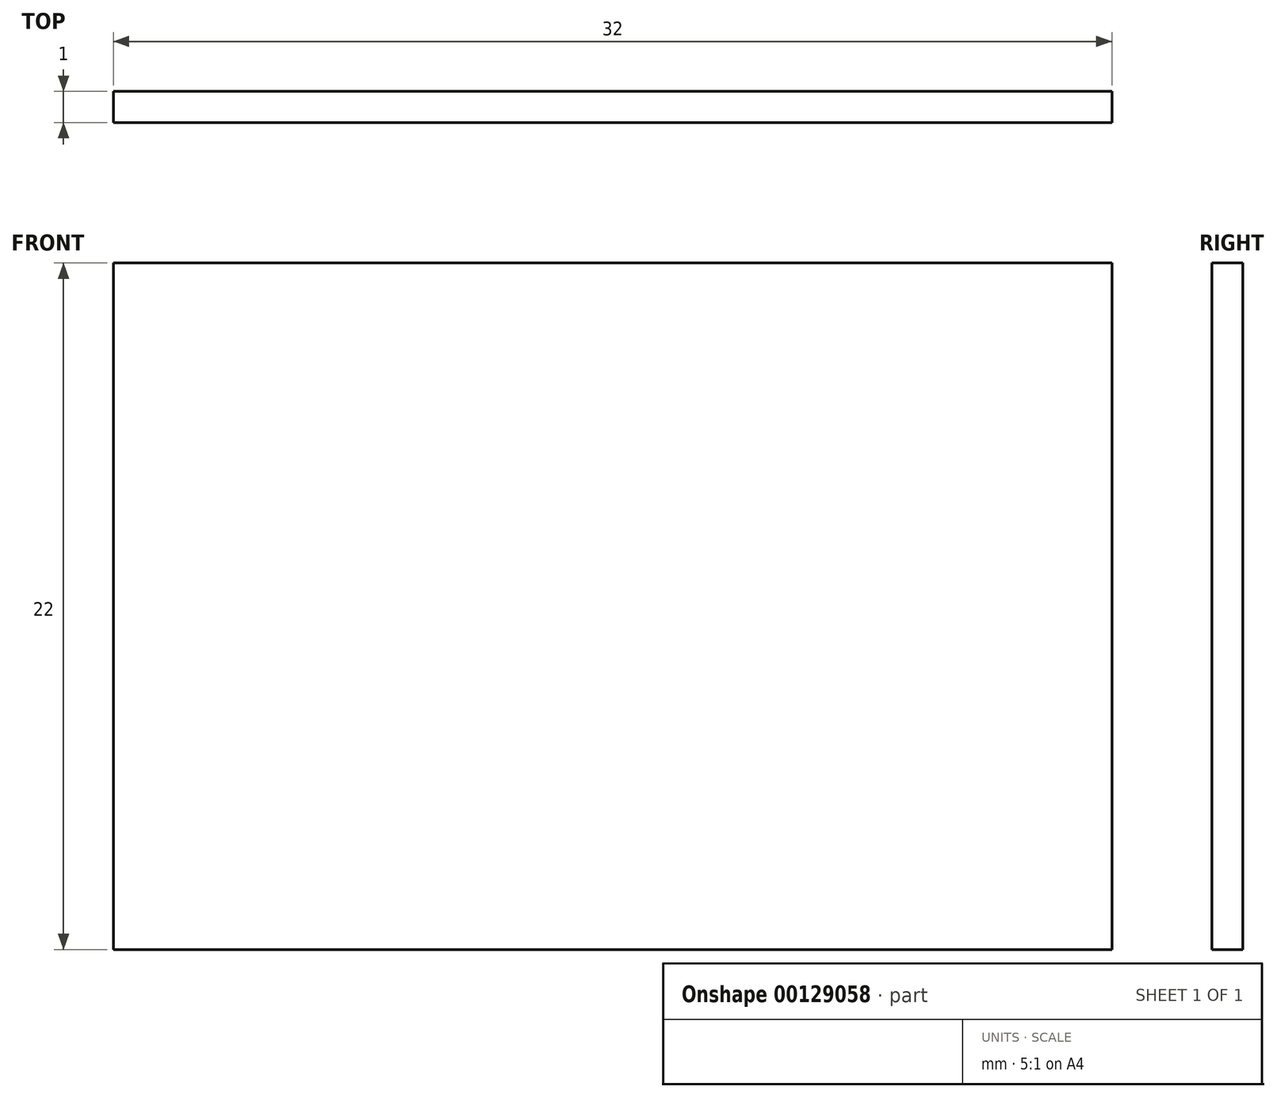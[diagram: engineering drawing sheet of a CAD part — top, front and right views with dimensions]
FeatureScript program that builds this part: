
annotation { "Feature Type Name" : "Feature", "Feature Type Description" : "" }
export const myFeature = defineFeature(function(context is Context, id is Id, definition is map)
    precondition{}
    {
        {
            var Q0;
            Q0=qCreatedBy(makeId("Front.planeOp"),FACE);
            var sketch = newSketch(context, id + "F0", { "sketchPlane" : qUnion([Q0])});
            skLineSegment(sketch, "E0.bottom", {"start": v(0, 0) * mm, "end": v(32, 0) * mm});
            skLineSegment(sketch, "E0.top", {"start": v(0, 22) * mm, "end": v(32, 22) * mm});
            skLineSegment(sketch, "E0.left", {"start": v(0, 0) * mm, "end": v(0, 22) * mm});
            skLineSegment(sketch, "E0.right", {"start": v(32, 0) * mm, "end": v(32, 22) * mm});
            skSolve(sketch);
        }
        {
            var Q0;
            Q0=makeQuery(id+"F0.imprint","IMPRINT",FACE,{"disambiguationData":[TD([[makeQuery(id+"F0.imprint","IMPRINT",EDGE,{"derivedFrom":sQuery(id+"F0.wireOp",EDGE,"E0.bottom")}),1.0]])]});
            extrude(context, id + "F1", {"entities" : qUnion([Q0]), "depth" : 1 * mm});
        }
    });
